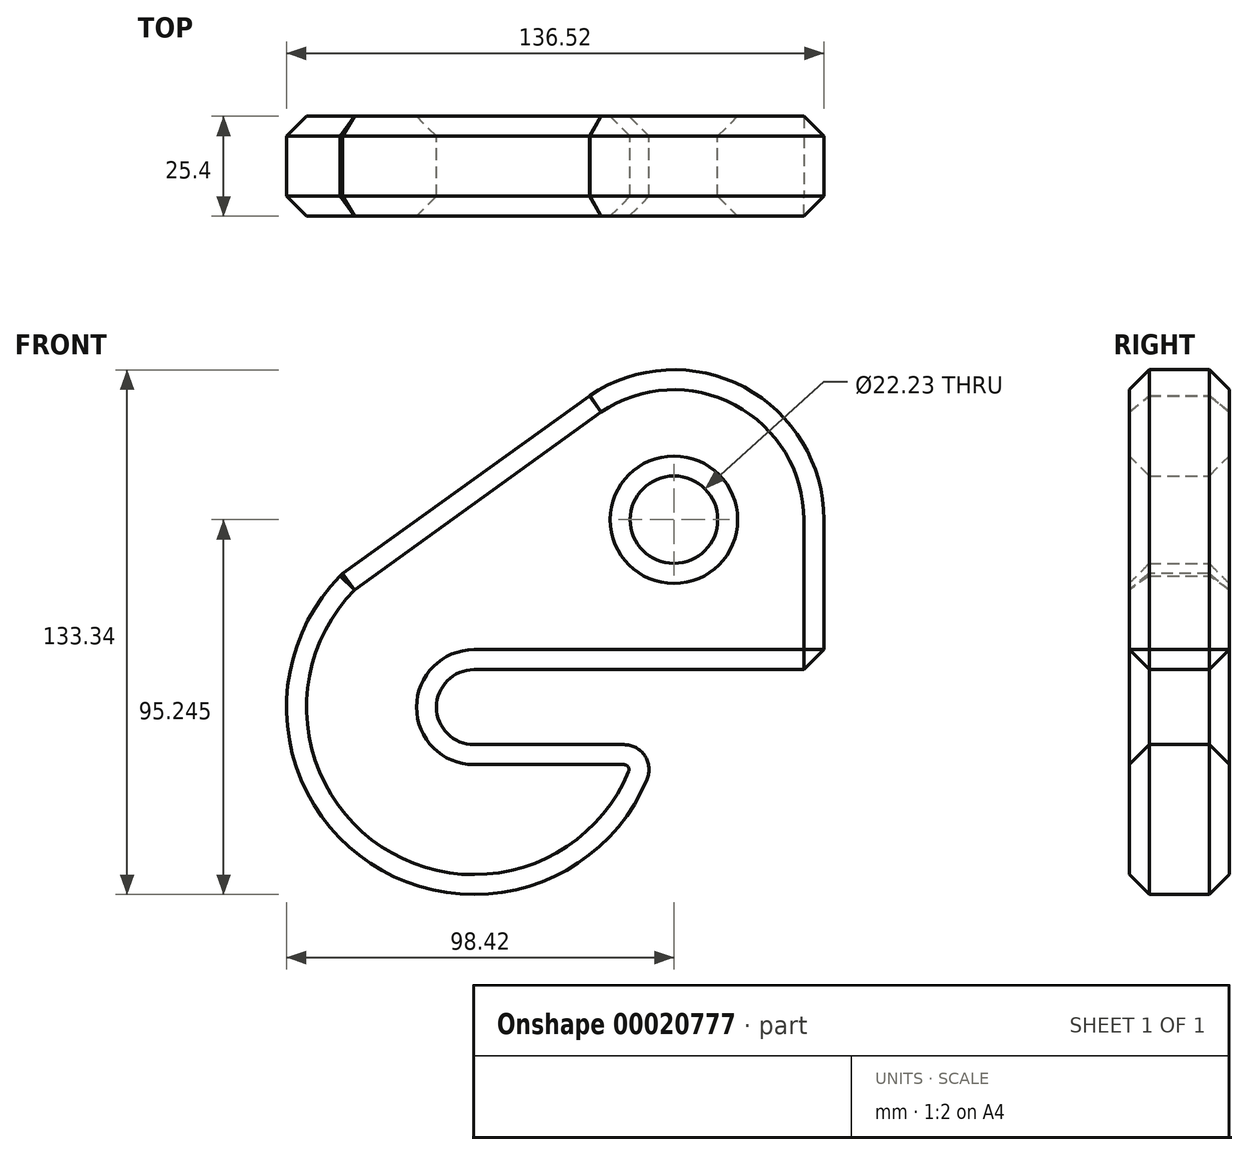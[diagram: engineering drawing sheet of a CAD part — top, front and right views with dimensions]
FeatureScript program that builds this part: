
annotation { "Feature Type Name" : "Feature", "Feature Type Description" : "" }
export const myFeature = defineFeature(function(context is Context, id is Id, definition is map)
    precondition{}
    {
        {
            var Q0;
            Q0=qCreatedBy(makeId("Front.planeOp"),FACE);
            var sketch = newSketch(context, id + "F0", { "sketchPlane" : qUnion([Q0])});
            skArc(sketch, "E0", {"start": v(0, 9.53) * mm, "mid": v(-9.53, 0) * mm, "end": v(0, -9.53) * mm});
            skArc(sketch, "E1", {"start": v(0, -47.63) * mm, "mid": v(26.42, -39.63) * mm, "end": v(43.96, -18.32) * mm});
            skLineSegment(sketch, "E2", {"start": v(0, 47.63) * mm, "end": v(0, 47.63) * mm});
            skLineSegment(sketch, "E3", {"start": v(0, -9.53) * mm, "end": v(38.1, -9.53) * mm});
            skLineSegment(sketch, "E4.bottom", {"start": v(0, 9.53) * mm, "end": v(88.9, 9.53) * mm});
            skLineSegment(sketch, "E4.right", {"start": v(88.9, 9.52) * mm, "end": v(88.9, 47.63) * mm});
            skArc(sketch, "E5.filletArc", {"start": v(43.96, -18.32) * mm, "mid": v(43.38, -12.35) * mm, "end": v(38.1, -9.53) * mm});
            skCircle(sketch, "E6", {"center": v(50.8, 47.63) * mm, "radius": 11.11 * mm});
            skLineSegment(sketch, "E7.bottom", {"start": v(0, 0) * mm, "end": v(-33.68, 0) * mm});
            skLineSegment(sketch, "E7.left", {"start": v(0, 0) * mm, "end": v(0, 33.68) * mm});
            skArc(sketch, "E8", {"start": v(-33.68, 33.68) * mm, "mid": v(-44, -18.23) * mm, "end": v(0, -47.63) * mm});
            skArc(sketch, "E9", {"start": v(88.9, 47.63) * mm, "mid": v(68.62, 81.3) * mm, "end": v(29.36, 79.12) * mm});
            skLineSegment(sketch, "E10", {"start": v(50.8, 9.53) * mm, "end": v(50.8, 9.53) * mm});
            skLineSegment(sketch, "E11", {"start": v(-33.68, 33.68) * mm, "end": v(29.36, 79.12) * mm});
            skSolve(sketch);
        }
        {
            var Q0;
            Q0=makeQuery(id+"F0.imprint","IMPRINT",FACE,{"disambiguationData":[TD([[makeQuery(id+"F0.imprint","IMPRINT",EDGE,{"derivedFrom":sQuery(id+"F0.wireOp",EDGE,"E1")}),1.0]])]});
            extrude(context, id + "F1", {"entities" : qUnion([Q0]), "depth" : 25.4 * mm});
        }
        {
            var Q0;
            Q0=makeQuery(id+"F1.opExtrude","CAP_EDGE",EDGE,{"disambiguationData":[OSD([sQuery(id+"F0.wireOp",EDGE,"E9")])],"isStart":false});
            var Q1;
            Q1=makeQuery(id+"F1.opExtrude","SWEPT_EDGE",EDGE,{"disambiguationData":[OSD([sQuery(id+"F0.wireOp",EDGE,"E8"),sQuery(id+"F0.wireOp",EDGE,"E11")])]});
            var Q2;
            Q2=makeQuery(id+"F1.opExtrude","CAP_EDGE",EDGE,{"disambiguationData":[OSD([sQuery(id+"F0.wireOp",EDGE,"E11")])],"isStart":true});
            var Q3;
            Q3=makeQuery(id+"F1.opExtrude","CAP_EDGE",EDGE,{"disambiguationData":[OSD([sQuery(id+"F0.wireOp",EDGE,"E4.bottom")])],"isStart":false});
            var Q4;
            Q4=makeQuery(id+"F1.opExtrude","CAP_EDGE",EDGE,{"disambiguationData":[OSD([sQuery(id+"F0.wireOp",EDGE,"E4.right")])],"isStart":false});
            var Q5;
            Q5=makeQuery(id+"F1.opExtrude","CAP_EDGE",EDGE,{"disambiguationData":[OSD([sQuery(id+"F0.wireOp",EDGE,"E1"),sQuery(id+"F0.wireOp",EDGE,"E8")])],"isStart":false});
            var Q6;
            Q6=makeQuery(id+"F1.opExtrude","CAP_EDGE",EDGE,{"disambiguationData":[OSD([sQuery(id+"F0.wireOp",EDGE,"E1"),sQuery(id+"F0.wireOp",EDGE,"E8")])],"isStart":true});
            var Q7;
            Q7=makeQuery(id+"F1.opExtrude","CAP_EDGE",EDGE,{"disambiguationData":[OSD([sQuery(id+"F0.wireOp",EDGE,"E6")])],"isStart":false});
            var Q8;
            Q8=makeQuery(id+"F1.opExtrude","CAP_EDGE",EDGE,{"disambiguationData":[OSD([sQuery(id+"F0.wireOp",EDGE,"E9")])],"isStart":true});
            var Q9;
            Q9=makeQuery(id+"F1.opExtrude","SWEPT_EDGE",EDGE,{"disambiguationData":[OSD([sQuery(id+"F0.wireOp",EDGE,"E4.bottom"),sQuery(id+"F0.wireOp",EDGE,"E4.right")])]});
            var Q10;
            Q10=makeQuery(id+"F1.opExtrude","CAP_EDGE",EDGE,{"disambiguationData":[OSD([sQuery(id+"F0.wireOp",EDGE,"E11")])],"isStart":false});
            var Q11;
            Q11=makeQuery(id+"F1.opExtrude","CAP_EDGE",EDGE,{"disambiguationData":[OSD([sQuery(id+"F0.wireOp",EDGE,"E4.right")])],"isStart":true});
            var Q12;
            Q12=makeQuery(id+"F1.opExtrude","CAP_EDGE",EDGE,{"disambiguationData":[OSD([sQuery(id+"F0.wireOp",EDGE,"E3")])],"isStart":true});
            var Q13;
            Q13=makeQuery(id+"F1.opExtrude","CAP_EDGE",EDGE,{"disambiguationData":[OSD([sQuery(id+"F0.wireOp",EDGE,"E5.filletArc")])],"isStart":true});
            var Q14;
            Q14=makeQuery(id+"F1.opExtrude","CAP_EDGE",EDGE,{"disambiguationData":[OSD([sQuery(id+"F0.wireOp",EDGE,"E5.filletArc")])],"isStart":false});
            var Q15;
            Q15=makeQuery(id+"F1.opExtrude","CAP_EDGE",EDGE,{"disambiguationData":[OSD([sQuery(id+"F0.wireOp",EDGE,"E0")])],"isStart":false});
            var Q16;
            Q16=makeQuery(id+"F1.opExtrude","CAP_EDGE",EDGE,{"disambiguationData":[OSD([sQuery(id+"F0.wireOp",EDGE,"E6")])],"isStart":true});
            var Q17;
            Q17=makeQuery(id+"F1.opExtrude","CAP_EDGE",EDGE,{"disambiguationData":[OSD([sQuery(id+"F0.wireOp",EDGE,"E0")])],"isStart":true});
            var Q18;
            Q18=makeQuery(id+"F1.opExtrude","SWEPT_EDGE",EDGE,{"disambiguationData":[OSD([sQuery(id+"F0.wireOp",EDGE,"E9"),sQuery(id+"F0.wireOp",EDGE,"E11")])]});
            var Q19;
            Q19=makeQuery(id+"F1.opExtrude","SWEPT_EDGE",EDGE,{"disambiguationData":[OSD([sQuery(id+"F0.wireOp",EDGE,"E4.right"),sQuery(id+"F0.wireOp",EDGE,"E9")])]});
            var Q20;
            Q20=makeQuery(id+"F1.opExtrude","SWEPT_EDGE",EDGE,{"disambiguationData":[OSD([sQuery(id+"F0.wireOp",EDGE,"E0"),sQuery(id+"F0.wireOp",EDGE,"E3")])]});
            var Q21;
            Q21=makeQuery(id+"F1.opExtrude","SWEPT_EDGE",EDGE,{"disambiguationData":[OSD([sQuery(id+"F0.wireOp",EDGE,"E0"),sQuery(id+"F0.wireOp",EDGE,"E4.bottom"),sQuery(id+"F0.wireOp",EDGE,"E7.left")])]});
            var Q22;
            Q22=makeQuery(id+"F1.opExtrude","CAP_EDGE",EDGE,{"disambiguationData":[OSD([sQuery(id+"F0.wireOp",EDGE,"E3")])],"isStart":false});
            var Q23;
            Q23=makeQuery(id+"F1.opExtrude","SWEPT_EDGE",EDGE,{"disambiguationData":[OSD([sQuery(id+"F0.wireOp",EDGE,"E3"),sQuery(id+"F0.wireOp",EDGE,"E5.filletArc")])]});
            var Q24;
            Q24=makeQuery(id+"F1.opExtrude","SWEPT_EDGE",EDGE,{"disambiguationData":[OSD([sQuery(id+"F0.wireOp",EDGE,"E1"),sQuery(id+"F0.wireOp",EDGE,"E5.filletArc")])]});
            var Q25;
            Q25=makeQuery(id+"F1.opExtrude","CAP_EDGE",EDGE,{"disambiguationData":[OSD([sQuery(id+"F0.wireOp",EDGE,"E4.bottom")])],"isStart":true});
            chamfer(context, id + "F2", {"entities" : qUnion([Q0, Q1, Q2, Q3, Q4, Q5, Q6, Q7, Q8, Q9, Q10, Q11, Q12, Q13, Q14, Q15, Q16, Q17, Q18, Q19, Q20, Q21, Q22, Q23, Q24, Q25]), "width" : 5.08 * mm, "tangentPropagation" : true});
        }
    });
